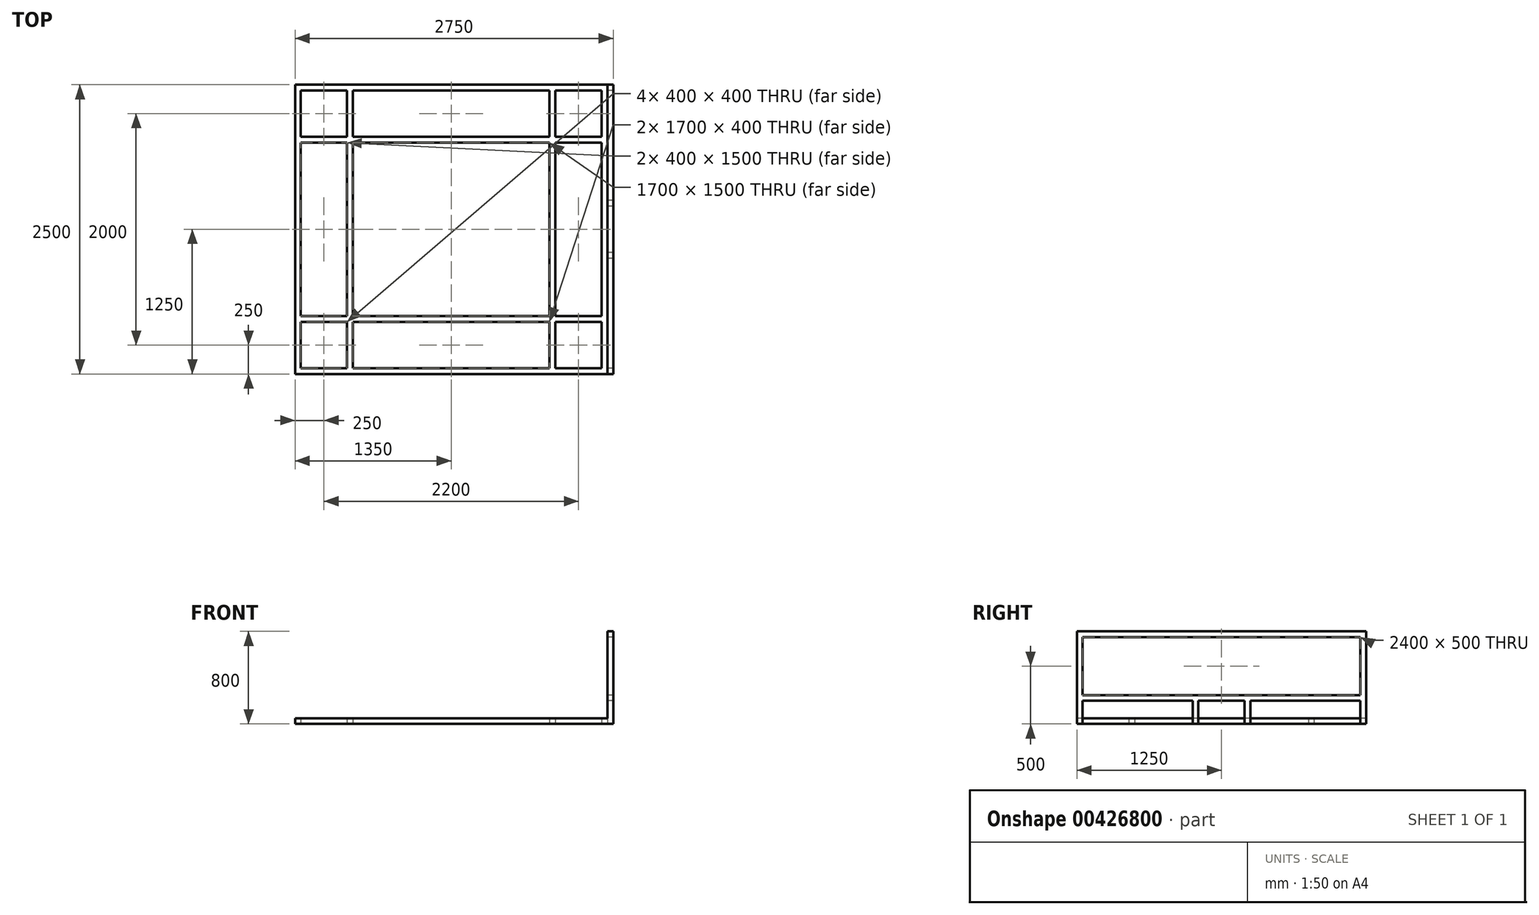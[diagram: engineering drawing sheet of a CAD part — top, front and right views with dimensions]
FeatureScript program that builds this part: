
annotation { "Feature Type Name" : "Feature", "Feature Type Description" : "" }
export const myFeature = defineFeature(function(context is Context, id is Id, definition is map)
    precondition{}
    {
        {
            var Q0;
            Q0=qCreatedBy(makeId("Top.planeOp"),FACE);
            var sketch = newSketch(context, id + "F0", { "sketchPlane" : qUnion([Q0])});
            skLineSegment(sketch, "E0.bottom", {"start": v(1350, 1250) * mm, "end": v(-1350, 1250) * mm});
            skLineSegment(sketch, "E0.top", {"start": v(1350, -1250) * mm, "end": v(-1350, -1250) * mm});
            skLineSegment(sketch, "E0.left", {"start": v(1350, 1250) * mm, "end": v(1350, -1250) * mm});
            skLineSegment(sketch, "E0.right", {"start": v(-1350, 1250) * mm, "end": v(-1350, -1250) * mm});
            skPoint(sketch, "E0.middle", {"position": v(0, 0) * mm});
            skLineSegment(sketch, "E1.bottom", {"start": v(1300, 1200) * mm, "end": v(-1300, 1200) * mm});
            skLineSegment(sketch, "E1.top", {"start": v(1300, -1200) * mm, "end": v(-1300, -1200) * mm});
            skLineSegment(sketch, "E1.left", {"start": v(1300, 1200) * mm, "end": v(1300, -1200) * mm});
            skLineSegment(sketch, "E1.right", {"start": v(-1300, 1200) * mm, "end": v(-1300, -1200) * mm});
            skLineSegment(sketch, "E2", {"start": v(-1300, 800) * mm, "end": v(1300, 800) * mm});
            skLineSegment(sketch, "E3", {"start": v(-1300, 750) * mm, "end": v(1300, 750) * mm});
            skLineSegment(sketch, "E4", {"start": v(-1300, -800) * mm, "end": v(1300, -800) * mm});
            skLineSegment(sketch, "E5", {"start": v(-1300, -750) * mm, "end": v(1300, -750) * mm});
            skLineSegment(sketch, "E6", {"start": v(-900, 1200) * mm, "end": v(-900, 800) * mm});
            skLineSegment(sketch, "E7", {"start": v(-850, 1200) * mm, "end": v(-850, 800) * mm});
            skLineSegment(sketch, "E8", {"start": v(900, 1200) * mm, "end": v(900, 800) * mm});
            skLineSegment(sketch, "E9", {"start": v(850, 1200) * mm, "end": v(850, 800) * mm});
            skLineSegment(sketch, "E10.trimOffspring", {"start": v(-900, 750) * mm, "end": v(-900, -750) * mm});
            skLineSegment(sketch, "E11.trimOffspring", {"start": v(-850, 750) * mm, "end": v(-850, -750) * mm});
            skLineSegment(sketch, "E12.trimOffspring", {"start": v(850, 750) * mm, "end": v(850, -750) * mm});
            skLineSegment(sketch, "E13.trimOffspring", {"start": v(900, 750) * mm, "end": v(900, -750) * mm});
            skLineSegment(sketch, "E14.trimOffspring", {"start": v(850, -800) * mm, "end": v(850, -1200) * mm});
            skLineSegment(sketch, "E15.trimOffspring", {"start": v(900, -800) * mm, "end": v(900, -1200) * mm});
            skLineSegment(sketch, "E16.trimOffspring", {"start": v(-900, -800) * mm, "end": v(-900, -1200) * mm});
            skLineSegment(sketch, "E17.trimOffspring", {"start": v(-850, -800) * mm, "end": v(-850, -1200) * mm});
            skSolve(sketch);
        }
        {
            var Q0;
            Q0=makeQuery(id+"F0.imprint","IMPRINT",FACE,{"disambiguationData":[TD([[makeQuery(id+"F0.imprint","IMPRINT",EDGE,{"derivedFrom":sQuery(id+"F0.wireOp",EDGE,"E0.bottom")}),1.0]])]});
            var Q1;
            {var subQ0=sQuery(id+"F0.wireOp",EDGE,"E6");Q1=makeQuery(id+"F0.imprint","IMPRINT",FACE,{"disambiguationData":[TD([[makeQuery(id+"F0.imprint","IMPRINT",EDGE,{"derivedFrom":subQ0}),1.0]])]});}
            var Q2;
            {var subQ5=sQuery(id+"F0.wireOp",EDGE,"E2");var subQ6=sQuery(id+"F0.wireOp",EDGE,"E1.left");var subQ7=makeQuery(id+"F0.imprint","INTERSECT",VERTEX,{"derivedFrom":[subQ6,subQ5]});Q2=makeQuery(id+"F0.imprint","IMPRINT",FACE,{"disambiguationData":[TD([[makeQuery(id+"F0.imprint","IMPRINT",EDGE,{"disambiguationData":[TD([[subQ7,-1.0]])],"derivedFrom":subQ6}),-1.0]])]});}
            var Q3;
            {var subQ0=sQuery(id+"F0.wireOp",EDGE,"E10.trimOffspring");Q3=makeQuery(id+"F0.imprint","IMPRINT",FACE,{"disambiguationData":[TD([[makeQuery(id+"F0.imprint","IMPRINT",EDGE,{"derivedFrom":subQ0}),1.0]])]});}
            var Q4;
            {var subQ0=sQuery(id+"F0.wireOp",EDGE,"E8");Q4=makeQuery(id+"F0.imprint","IMPRINT",FACE,{"disambiguationData":[TD([[makeQuery(id+"F0.imprint","IMPRINT",EDGE,{"derivedFrom":subQ0}),-1.0]])]});}
            var Q5;
            {var subQ4=sQuery(id+"F0.wireOp",EDGE,"E4");var subQ5=sQuery(id+"F0.wireOp",EDGE,"E1.left");var subQ6=makeQuery(id+"F0.imprint","INTERSECT",VERTEX,{"derivedFrom":[subQ5,subQ4]});Q5=makeQuery(id+"F0.imprint","IMPRINT",FACE,{"disambiguationData":[TD([[makeQuery(id+"F0.imprint","IMPRINT",EDGE,{"disambiguationData":[TD([[subQ6,1.0]])],"derivedFrom":subQ5}),-1.0]])]});}
            var Q6;
            {var subQ0=sQuery(id+"F0.wireOp",EDGE,"E12.trimOffspring");Q6=makeQuery(id+"F0.imprint","IMPRINT",FACE,{"disambiguationData":[TD([[makeQuery(id+"F0.imprint","IMPRINT",EDGE,{"derivedFrom":subQ0}),1.0]])]});}
            var Q7;
            {var subQ0=sQuery(id+"F0.wireOp",EDGE,"E14.trimOffspring");Q7=makeQuery(id+"F0.imprint","IMPRINT",FACE,{"disambiguationData":[TD([[makeQuery(id+"F0.imprint","IMPRINT",EDGE,{"derivedFrom":subQ0}),1.0]])]});}
            var Q8;
            {var subQ0=sQuery(id+"F0.wireOp",EDGE,"E16.trimOffspring");Q8=makeQuery(id+"F0.imprint","IMPRINT",FACE,{"disambiguationData":[TD([[makeQuery(id+"F0.imprint","IMPRINT",EDGE,{"derivedFrom":subQ0}),1.0]])]});}
            extrude(context, id + "F1", {"entities" : qUnion([Q0, Q1, Q2, Q3, Q4, Q5, Q6, Q7, Q8]), "depth" : 50 * mm});
        }
        {
            var Q0;
            Q0=makeQuery(id+"F1.opExtrude","SWEPT_FACE",FACE,{"disambiguationData":[OSD([sQuery(id+"F0.wireOp",EDGE,"E0.left")])]});
            var sketch = newSketch(context, id + "F2", { "sketchPlane" : qUnion([Q0])});
            skLineSegment(sketch, "E18", {"start": v(-1250, 0) * mm, "end": v(-1250, 800) * mm});
            skLineSegment(sketch, "E19", {"start": v(-1250, 800) * mm, "end": v(1250, 800) * mm});
            skLineSegment(sketch, "E20", {"start": v(1250, 800) * mm, "end": v(1250, 0) * mm});
            skLineSegment(sketch, "E21", {"start": v(1250, 0) * mm, "end": v(1200, 0) * mm});
            skLineSegment(sketch, "E22", {"start": v(1200, 0) * mm, "end": v(1200, 750) * mm});
            skLineSegment(sketch, "E23", {"start": v(1200, 750) * mm, "end": v(-1200, 750) * mm});
            skLineSegment(sketch, "E24", {"start": v(-1200, 750) * mm, "end": v(-1200, 0) * mm});
            skLineSegment(sketch, "E25", {"start": v(-1200, 0) * mm, "end": v(-1250, 0) * mm});
            skLineSegment(sketch, "E26", {"start": v(-1200, 250) * mm, "end": v(1200, 250) * mm});
            skLineSegment(sketch, "E27", {"start": v(1200, 250) * mm, "end": v(1200, 200) * mm});
            skLineSegment(sketch, "E28", {"start": v(1200, 200) * mm, "end": v(-1200, 200) * mm});
            skLineSegment(sketch, "E29", {"start": v(-250, 200) * mm, "end": v(-250, 0) * mm});
            skLineSegment(sketch, "E30", {"start": v(-250, 0) * mm, "end": v(-200, 0) * mm});
            skLineSegment(sketch, "E31", {"start": v(-200, 0) * mm, "end": v(-200, 200) * mm});
            skLineSegment(sketch, "E32", {"start": v(200, 200) * mm, "end": v(200, 0) * mm});
            skLineSegment(sketch, "E33", {"start": v(200, 0) * mm, "end": v(250, 0) * mm});
            skLineSegment(sketch, "E34", {"start": v(250, 0) * mm, "end": v(250, 200) * mm});
            skSolve(sketch);
        }
        {
            var Q0;
            {var subQ0=sQuery(id+"F2.wireOp",EDGE,"E25");Q0=makeQuery(id+"F2.imprint","IMPRINT",FACE,{"disambiguationData":[TD([[makeQuery(id+"F2.imprint","IMPRINT",EDGE,{"derivedFrom":subQ0}),-1.0]])]});}
            var Q1;
            {var subQ0=sQuery(id+"F2.wireOp",EDGE,"E21");Q1=makeQuery(id+"F2.imprint","IMPRINT",FACE,{"disambiguationData":[TD([[makeQuery(id+"F2.imprint","IMPRINT",EDGE,{"derivedFrom":subQ0}),-1.0]])]});}
            var Q2;
            {var subQ3=sQuery(id+"F2.wireOp",EDGE,"E19");Q2=makeQuery(id+"F2.imprint","IMPRINT",FACE,{"disambiguationData":[TD([[makeQuery(id+"F2.imprint","IMPRINT",EDGE,{"derivedFrom":subQ3}),-1.0]])]});}
            var Q3;
            {var subQ3=sQuery(id+"F2.wireOp",EDGE,"E26");Q3=makeQuery(id+"F2.imprint","IMPRINT",FACE,{"disambiguationData":[TD([[makeQuery(id+"F2.imprint","IMPRINT",EDGE,{"derivedFrom":subQ3}),-1.0]])]});}
            var Q4;
            {var subQ0=sQuery(id+"F2.wireOp",EDGE,"E29");var subQ1=sQuery(id+"F2.wireOp",EDGE,"E28");var subQ2=makeQuery(id+"F2.imprint","INTERSECT",VERTEX,{"derivedFrom":[subQ1,subQ0]});Q4=makeQuery(id+"F2.imprint","IMPRINT",FACE,{"disambiguationData":[TD([[makeQuery(id+"F2.imprint","IMPRINT",EDGE,{"disambiguationData":[TD([[subQ2,1.0]])],"derivedFrom":subQ1}),1.0]])]});}
            var Q5;
            {var subQ0=sQuery(id+"F2.wireOp",EDGE,"E32");var subQ1=sQuery(id+"F2.wireOp",EDGE,"E28");var subQ2=makeQuery(id+"F2.imprint","INTERSECT",VERTEX,{"derivedFrom":[subQ1,subQ0]});Q5=makeQuery(id+"F2.imprint","IMPRINT",FACE,{"disambiguationData":[TD([[makeQuery(id+"F2.imprint","IMPRINT",EDGE,{"disambiguationData":[TD([[subQ2,1.0]])],"derivedFrom":subQ1}),1.0]])]});}
            var Q6;
            {var subQ0=sQuery(id+"F2.wireOp",EDGE,"E33");Q6=makeQuery(id+"F2.imprint","IMPRINT",FACE,{"disambiguationData":[TD([[makeQuery(id+"F2.imprint","IMPRINT",EDGE,{"derivedFrom":subQ0}),-1.0]])]});}
            var Q7;
            {var subQ0=sQuery(id+"F2.wireOp",EDGE,"E30");Q7=makeQuery(id+"F2.imprint","IMPRINT",FACE,{"disambiguationData":[TD([[makeQuery(id+"F2.imprint","IMPRINT",EDGE,{"derivedFrom":subQ0}),-1.0]])]});}
            extrude(context, id + "F3", {"entities" : qUnion([Q0, Q1, Q2, Q3, Q4, Q5, Q6, Q7]), "operationType" : NewBodyOperationType.ADD, "depth" : 50 * mm});
        }
    });
